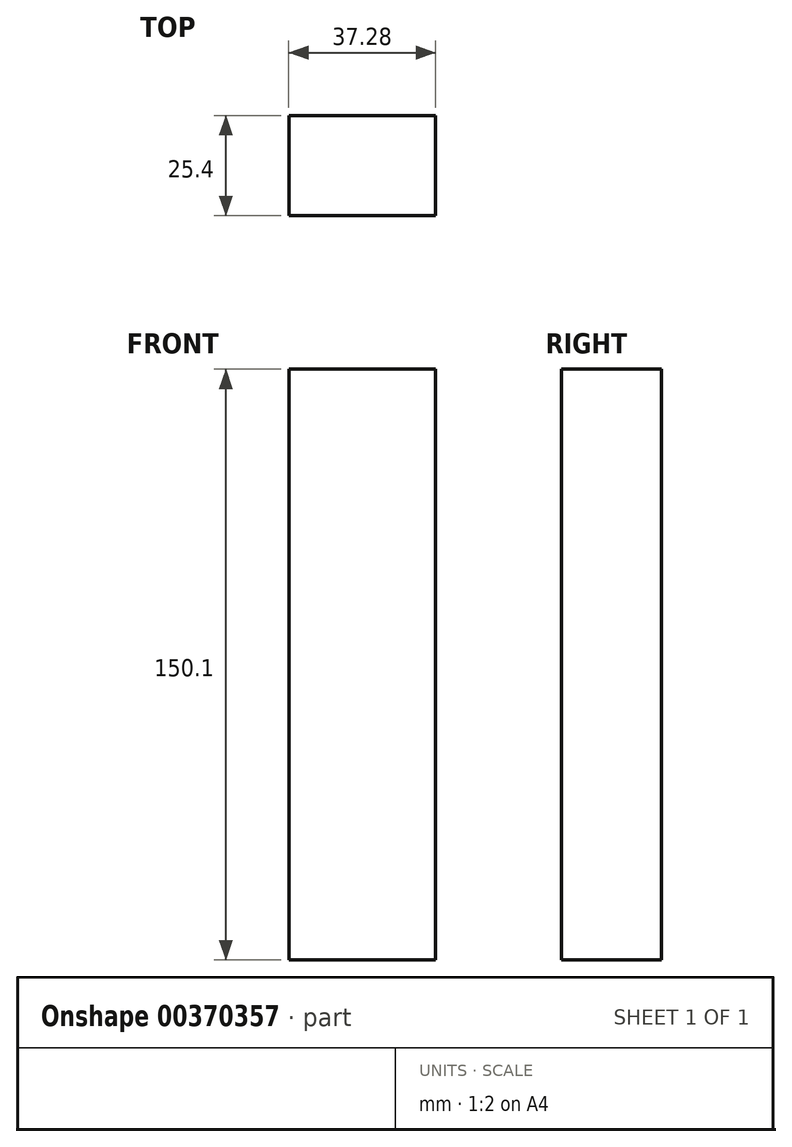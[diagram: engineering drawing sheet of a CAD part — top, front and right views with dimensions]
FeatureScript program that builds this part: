
annotation { "Feature Type Name" : "Feature", "Feature Type Description" : "" }
export const myFeature = defineFeature(function(context is Context, id is Id, definition is map)
    precondition{}
    {
        {
            var Q0;
            Q0=qCreatedBy(makeId("Front.planeOp"),FACE);
            var sketch = newSketch(context, id + "F0", { "sketchPlane" : qUnion([Q0])});
            skLineSegment(sketch, "E0.bottom", {"start": v(-18.7, 74.3) * mm, "end": v(18.58, 74.3) * mm});
            skLineSegment(sketch, "E0.top", {"start": v(-18.7, -75.8) * mm, "end": v(18.58, -75.8) * mm});
            skLineSegment(sketch, "E0.left", {"start": v(-18.7, 74.3) * mm, "end": v(-18.7, -75.8) * mm});
            skLineSegment(sketch, "E0.right", {"start": v(18.58, 74.3) * mm, "end": v(18.58, -75.8) * mm});
            skSolve(sketch);
        }
        {
            var Q0;
            Q0=makeQuery(id+"F0.imprint","IMPRINT",FACE,{"disambiguationData":[TD([[makeQuery(id+"F0.imprint","IMPRINT",EDGE,{"derivedFrom":sQuery(id+"F0.wireOp",EDGE,"E0.bottom")}),-1.0]])]});
            extrude(context, id + "F1", {"entities" : qUnion([Q0]), "depth" : 25.4 * mm});
        }
    });
